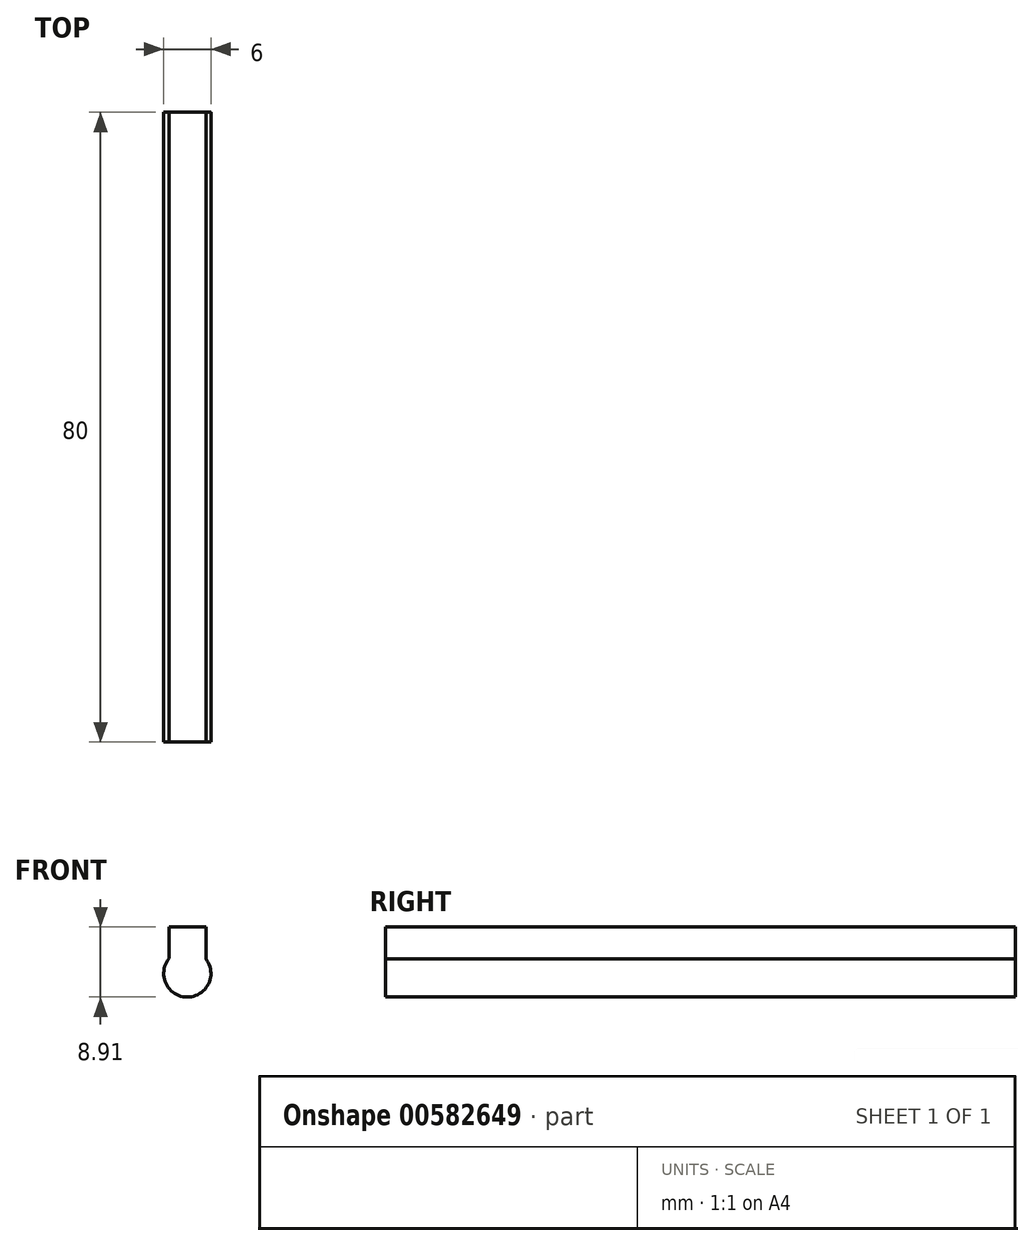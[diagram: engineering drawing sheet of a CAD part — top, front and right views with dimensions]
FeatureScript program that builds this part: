
annotation { "Feature Type Name" : "Feature", "Feature Type Description" : "" }
export const myFeature = defineFeature(function(context is Context, id is Id, definition is map)
    precondition{}
    {
        {
            var Q0;
            Q0=qCreatedBy(makeId("Front.planeOp"),FACE);
            var sketch = newSketch(context, id + "F0", { "sketchPlane" : qUnion([Q0])});
            skCircle(sketch, "E0", {"center": v(0, 0) * mm, "radius": 3 * mm});
            skLineSegment(sketch, "E1", {"start": v(-2.33, 1.89) * mm, "end": v(-2.33, 5.89) * mm});
            skLineSegment(sketch, "E2", {"start": v(2.35, 1.86) * mm, "end": v(2.35, 5.91) * mm});
            skLineSegment(sketch, "E3", {"start": v(2.35, 5.91) * mm, "end": v(-2.33, 5.89) * mm});
            skSolve(sketch);
        }
        {
            var Q0;
            Q0=makeQuery(id+"F0.imprint","IMPRINT",FACE,{"disambiguationData":[TD([[makeQuery(id+"F0.imprint","IMPRINT",EDGE,{"derivedFrom":sQuery(id+"F0.wireOp",EDGE,"E0")}),1.0]])]});
            var Q1;
            {var subQ0=sQuery(id+"F0.wireOp",EDGE,"E1");Q1=makeQuery(id+"F0.imprint","IMPRINT",FACE,{"disambiguationData":[TD([[makeQuery(id+"F0.imprint","IMPRINT",EDGE,{"derivedFrom":subQ0}),-1.0]])]});}
            extrude(context, id + "F1", {"entities" : qUnion([Q0, Q1]), "depth" : 80 * mm, "offsetDistance" : 25 * mm});
        }
    });
